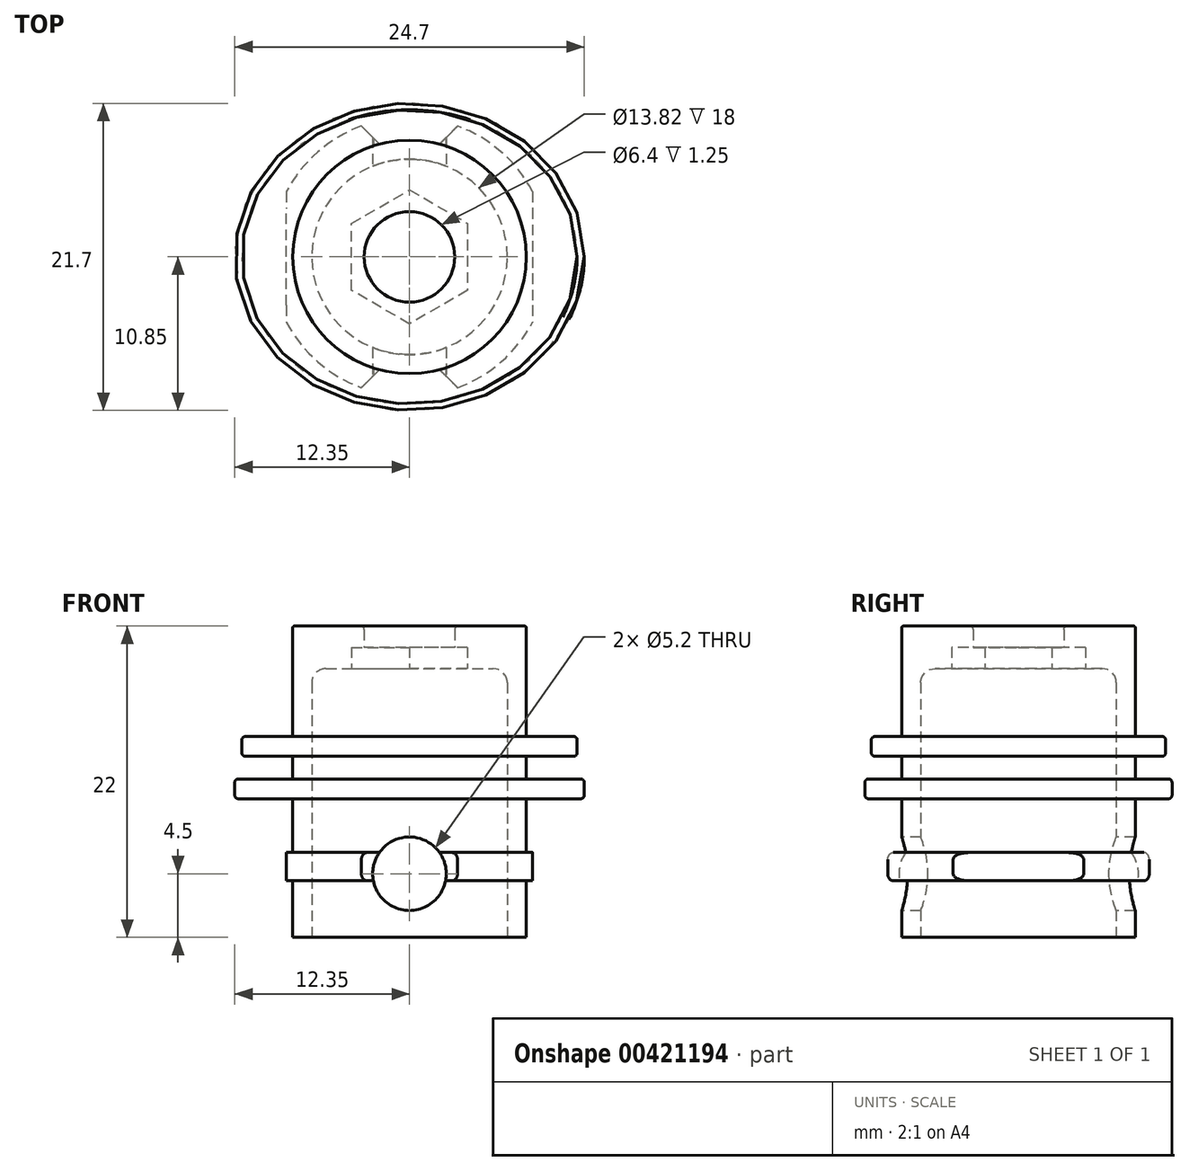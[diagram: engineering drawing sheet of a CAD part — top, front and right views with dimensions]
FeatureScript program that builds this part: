
annotation { "Feature Type Name" : "Feature", "Feature Type Description" : "" }
export const myFeature = defineFeature(function(context is Context, id is Id, definition is map)
    precondition{}
    {
        {
            var Q0;
            Q0=qCreatedBy(makeId("Front.planeOp"),FACE);
            var sketch = newSketch(context, id + "F0", { "sketchPlane" : qUnion([Q0])});
            skLineSegment(sketch, "E0", {"start": v(3.2, 19) * mm, "end": v(5.9, 19) * mm});
            skLineSegment(sketch, "E1", {"start": v(6.9, 18) * mm, "end": v(6.9, 0) * mm});
            skLineSegment(sketch, "E2", {"start": v(6.9, 0) * mm, "end": v(8.25, 0) * mm});
            skLineSegment(sketch, "E3", {"start": v(8.25, 0) * mm, "end": v(8.25, 4) * mm});
            skLineSegment(sketch, "E4", {"start": v(8.25, 4) * mm, "end": v(9.35, 4) * mm});
            skLineSegment(sketch, "E5", {"start": v(9.85, 4.5) * mm, "end": v(9.85, 5.5) * mm});
            skLineSegment(sketch, "E6", {"start": v(9.35, 6) * mm, "end": v(8.25, 6) * mm});
            skLineSegment(sketch, "E7", {"start": v(8.25, 6) * mm, "end": v(8.25, 9.8) * mm});
            skLineSegment(sketch, "E8", {"start": v(8.15, 22) * mm, "end": v(3.2, 22) * mm});
            skLineSegment(sketch, "E9", {"start": v(0, 19) * mm, "end": v(0, 22) * mm});
            skLineSegment(sketch, "E10", {"start": v(3.2, 22) * mm, "end": v(3.2, 19) * mm});
            skPoint(sketch, "E11.visualSharp", {"position": v(9.85, 6) * mm});
            skArc(sketch, "E11.filletArc", {"start": v(9.85, 5.5) * mm, "mid": v(9.7, 5.85) * mm, "end": v(9.35, 6) * mm});
            skPoint(sketch, "E12.visualSharp", {"position": v(9.85, 4) * mm});
            skArc(sketch, "E12.filletArc", {"start": v(9.35, 4) * mm, "mid": v(9.7, 4.15) * mm, "end": v(9.85, 4.5) * mm});
            skPoint(sketch, "E13.visualSharp", {"position": v(8.25, 22) * mm});
            skArc(sketch, "E13.filletArc", {"start": v(8.25, 21.9) * mm, "mid": v(8.22, 21.97) * mm, "end": v(8.15, 22) * mm});
            skPoint(sketch, "E14.visualSharp", {"position": v(6.9, 19) * mm});
            skArc(sketch, "E14.filletArc", {"start": v(6.9, 18) * mm, "mid": v(6.62, 18.7) * mm, "end": v(5.9, 19) * mm});
            skLineSegment(sketch, "E15", {"start": v(8.25, 9.8) * mm, "end": v(12.35, 9.8) * mm});
            skLineSegment(sketch, "E16", {"start": v(12.35, 9.8) * mm, "end": v(12.35, 11.2) * mm});
            skLineSegment(sketch, "E17", {"start": v(12.35, 11.2) * mm, "end": v(8.25, 11.2) * mm});
            skLineSegment(sketch, "E18.trimOffspring", {"start": v(8.25, 11.2) * mm, "end": v(8.25, 12.8) * mm});
            skLineSegment(sketch, "E19", {"start": v(8.25, 12.8) * mm, "end": v(11.85, 12.8) * mm});
            skLineSegment(sketch, "E20", {"start": v(11.85, 12.8) * mm, "end": v(11.85, 14.2) * mm});
            skLineSegment(sketch, "E21", {"start": v(11.85, 14.2) * mm, "end": v(8.25, 14.2) * mm});
            skLineSegment(sketch, "E22.trimOffspring", {"start": v(8.25, 14.2) * mm, "end": v(8.25, 21.9) * mm});
            skSolve(sketch);
        }
        {
            var Q0;
            Q0 = qSketchRegion(id + "F0", true);
            var Q1;
            Q1=sQuery(id+"F0.wireOp",EDGE,"E9");
            revolve(context, id + "F1", {"entities" : qUnion([Q0]), "axis" : qUnion([Q1]), "revolveType" : RevolveType.FULL});
        }
        {
            var Q0;
            Q0=qCreatedBy(makeId("Front.planeOp"),FACE);
            var sketch = newSketch(context, id + "F2", { "sketchPlane" : qUnion([Q0])});
            skPoint(sketch, "E23", {"position": v(0, 4.5) * mm});
            skCircle(sketch, "E24", {"center": v(0, 4.5) * mm, "radius": 2.6 * mm});
            skSolve(sketch);
        }
        {
            var Q0;
            Q0 = qSketchRegion(id + "F2", true);
            extrude(context, id + "F3", {"entities" : qUnion([Q0]), "operationType" : NewBodyOperationType.REMOVE, "oppositeDirection" : true, "depth" : 25 * mm, "hasSecondDirection" : true, "secondDirectionOppositeDirection" : false, "secondDirectionDepth" : 25 * mm});
        }
        {
            var Q0;
            Q0=qCreatedBy(makeId("Top.planeOp"),FACE);
            var sketch = newSketch(context, id + "F4", { "sketchPlane" : qUnion([Q0])});
            skLineSegment(sketch, "E25.left", {"start": v(-8.7, 12) * mm, "end": v(-8.7, -12) * mm});
            skLineSegment(sketch, "E25.right", {"start": v(8.7, 12) * mm, "end": v(8.7, -12) * mm});
            skPoint(sketch, "E25.middle", {"position": v(0, 0) * mm});
            skLineSegment(sketch, "E26", {"start": v(-8.7, 12) * mm, "end": v(-18.7, 12) * mm});
            skLineSegment(sketch, "E27", {"start": v(-18.7, -12) * mm, "end": v(-8.7, -12) * mm});
            skLineSegment(sketch, "E28", {"start": v(-18.7, 12) * mm, "end": v(-18.7, -12) * mm});
            skLineSegment(sketch, "E29", {"start": v(8.7, 12) * mm, "end": v(18.7, 12) * mm});
            skLineSegment(sketch, "E30", {"start": v(18.7, 12) * mm, "end": v(18.7, -12) * mm});
            skLineSegment(sketch, "E31", {"start": v(18.7, -12) * mm, "end": v(8.7, -12) * mm});
            skSolve(sketch);
        }
        {
            var Q0;
            Q0=makeQuery(id+"F4.imprint","IMPRINT",FACE,{"disambiguationData":[TD([[makeQuery(id+"F4.imprint","IMPRINT",EDGE,{"derivedFrom":sQuery(id+"F4.wireOp",EDGE,"E25.left")}),-1.0]])]});
            var Q1;
            Q1=makeQuery(id+"F4.imprint","IMPRINT",FACE,{"disambiguationData":[TD([[makeQuery(id+"F4.imprint","IMPRINT",EDGE,{"derivedFrom":sQuery(id+"F4.wireOp",EDGE,"E25.right")}),1.0]])]});
            extrude(context, id + "F5", {"entities" : qUnion([Q0, Q1]), "operationType" : NewBodyOperationType.REMOVE, "flatOperationType" : FlatOperationType.REMOVE, "offsetDistance" : 25 * mm, "depth" : 7 * mm, "domain" : OperationDomain.MODEL});
        }
        {
            var Q0;
            Q0=qCreatedBy(makeId("Top.planeOp"),FACE);
            var sketch = newSketch(context, id + "F6", { "sketchPlane" : qUnion([Q0])});
            skLineSegment(sketch, "E32", {"start": v(-2.12, 7.97) * mm, "end": v(-6.37, 12.21) * mm});
            skLineSegment(sketch, "E33", {"start": v(2.12, 7.97) * mm, "end": v(6.37, 12.21) * mm});
            skLineSegment(sketch, "E34", {"start": v(2.12, -7.97) * mm, "end": v(6.37, -12.21) * mm});
            skLineSegment(sketch, "E35", {"start": v(-2.12, -7.97) * mm, "end": v(-6.37, -12.21) * mm});
            skLineSegment(sketch, "E36", {"start": v(-6.37, 12.21) * mm, "end": v(6.37, 12.21) * mm});
            skLineSegment(sketch, "E37", {"start": v(-6.37, -12.21) * mm, "end": v(6.37, -12.21) * mm});
            skArc(sketch, "E38", {"start": v(2.12, 7.97) * mm, "mid": v(0, 8.25) * mm, "end": v(-2.12, 7.97) * mm});
            skArc(sketch, "E39", {"start": v(-2.12, -7.97) * mm, "mid": v(0, -8.25) * mm, "end": v(2.12, -7.97) * mm});
            skSolve(sketch);
        }
        {
            var Q0;
            Q0=makeQuery(id+"F6.imprint","IMPRINT",FACE,{"disambiguationData":[TD([[makeQuery(id+"F6.imprint","IMPRINT",EDGE,{"derivedFrom":sQuery(id+"F6.wireOp",EDGE,"E32")}),-1.0]])]});
            var Q1;
            Q1=makeQuery(id+"F6.imprint","IMPRINT",FACE,{"disambiguationData":[TD([[makeQuery(id+"F6.imprint","IMPRINT",EDGE,{"derivedFrom":sQuery(id+"F6.wireOp",EDGE,"E34")}),-1.0]])]});
            extrude(context, id + "F7", {"entities" : qUnion([Q0, Q1]), "operationType" : NewBodyOperationType.REMOVE, "depth" : 6 * mm});
        }
        {
            var Q0;
            Q0=qCreatedBy(makeId("Top.planeOp"),FACE);
            var sketch = newSketch(context, id + "F8", { "sketchPlane" : qUnion([Q0])});
            skCircle(sketch, "E40.cCircle", {"center": v(0, 0) * mm, "radius": 4.73 * mm, "construction": true});
            skLineSegment(sketch, "E40.0", {"start": v(4.1, -2.37) * mm, "end": v(0, -4.73) * mm});
            skLineSegment(sketch, "E40.1", {"start": v(0, -4.73) * mm, "end": v(-4.1, -2.37) * mm});
            skLineSegment(sketch, "E40.2", {"start": v(-4.1, -2.37) * mm, "end": v(-4.1, 2.37) * mm});
            skLineSegment(sketch, "E40.3", {"start": v(-4.1, 2.37) * mm, "end": v(0, 4.73) * mm});
            skLineSegment(sketch, "E40.4", {"start": v(0, 4.73) * mm, "end": v(4.1, 2.37) * mm});
            skLineSegment(sketch, "E40.5", {"start": v(4.1, 2.37) * mm, "end": v(4.1, -2.37) * mm});
            skSolve(sketch);
        }
        {
            var Q0;
            Q0 = qSketchRegion(id + "F8", true);
            extrude(context, id + "F9", {"entities" : qUnion([Q0]), "operationType" : NewBodyOperationType.REMOVE, "depth" : 20.5 * mm});
        }
        {
            var Q0;
            Q0=qCreatedBy(makeId("Top.planeOp"),FACE);
            var sketch = newSketch(context, id + "F10", { "sketchPlane" : qUnion([Q0])});
            skEllipse(sketch, "E41", {"center": v(0, 0) * mm, "majorRadius": 12.35 * mm, "minorRadius": 10.85 * mm, "majorAxis": v(1, 0)});
            skCircle(sketch, "E42", {"center": v(0, 0) * mm, "radius": 16.7 * mm});
            skSolve(sketch);
        }
        {
            var Q0;
            Q0=makeQuery(id+"F10.imprint","IMPRINT",FACE,{"disambiguationData":[TD([[makeQuery(id+"F10.imprint","IMPRINT",EDGE,{"derivedFrom":sQuery(id+"F10.wireOp",EDGE,"E41")}),-1.0]])]});
            extrude(context, id + "F11", {"entities" : qUnion([Q0]), "operationType" : NewBodyOperationType.REMOVE, "depth" : 12 * mm});
        }
        {
            var Q0;
            Q0=qCreatedBy(makeId("Top.planeOp"),FACE);
            var sketch = newSketch(context, id + "F12", { "sketchPlane" : qUnion([Q0])});
            skEllipse(sketch, "E43", {"center": v(0, 0) * mm, "majorRadius": 11.85 * mm, "minorRadius": 10.4 * mm, "majorAxis": v(1, 0)});
            skCircle(sketch, "E44", {"center": v(0, 0) * mm, "radius": 16.92 * mm});
            skSolve(sketch);
        }
        {
            var Q0;
            Q0=makeQuery(id+"F12.imprint","IMPRINT",FACE,{"disambiguationData":[TD([[makeQuery(id+"F12.imprint","IMPRINT",EDGE,{"derivedFrom":sQuery(id+"F12.wireOp",EDGE,"E43")}),-1.0]])]});
            extrude(context, id + "F13", {"entities" : qUnion([Q0]), "operationType" : NewBodyOperationType.REMOVE, "depth" : 25 * mm, "hasSecondDirection" : true, "secondDirectionOppositeDirection" : false, "secondDirectionDepth" : 12 * mm});
        }
        {
            var Q0;
            Q0=makeQuery(id+"F13.boolean.opBoolean","INTERSECT",EDGE,{"derivedFrom":[makeQuery(id+"F1.opRevolve","SWEPT_FACE",FACE,{"disambiguationData":[OSD([sQuery(id+"F0.wireOp",EDGE,"E21")])]}),makeQuery(id+"F13.opExtrude","SWEPT_FACE",FACE,{"disambiguationData":[OSD([sQuery(id+"F12.wireOp",EDGE,"E43")])]})]});
            var Q1;
            Q1=makeQuery(id+"F13.boolean.opBoolean","INTERSECT",EDGE,{"derivedFrom":[makeQuery(id+"F1.opRevolve","SWEPT_FACE",FACE,{"disambiguationData":[OSD([sQuery(id+"F0.wireOp",EDGE,"E19")])]}),makeQuery(id+"F13.opExtrude","SWEPT_FACE",FACE,{"disambiguationData":[OSD([sQuery(id+"F12.wireOp",EDGE,"E43")])]})]});
            var Q2;
            Q2=makeQuery(id+"F11.boolean.opBoolean","INTERSECT",EDGE,{"derivedFrom":[makeQuery(id+"F1.opRevolve","SWEPT_FACE",FACE,{"disambiguationData":[OSD([sQuery(id+"F0.wireOp",EDGE,"E17")])]}),makeQuery(id+"F11.opExtrude","SWEPT_FACE",FACE,{"disambiguationData":[OSD([sQuery(id+"F10.wireOp",EDGE,"E41")])]})]});
            var Q3;
            Q3=makeQuery(id+"F11.boolean.opBoolean","INTERSECT",EDGE,{"derivedFrom":[makeQuery(id+"F1.opRevolve","SWEPT_FACE",FACE,{"disambiguationData":[OSD([sQuery(id+"F0.wireOp",EDGE,"E15")])]}),makeQuery(id+"F11.opExtrude","SWEPT_FACE",FACE,{"disambiguationData":[OSD([sQuery(id+"F10.wireOp",EDGE,"E41")])]})]});
            fillet(context, id + "F14", {"entities" : qUnion([Q0, Q1, Q2, Q3]), "radius" : 0.25 * mm, "tangentPropagation" : true, "allowEdgeOverflow" : false});
        }
        {
            var Q0;
            Q0=makeQuery(id+"F1.opRevolve","SWEPT_EDGE",EDGE,{"disambiguationData":[OSD([sQuery(id+"F0.wireOp",EDGE,"E8"),sQuery(id+"F0.wireOp",EDGE,"E10")])]});
            fillet(context, id + "F15", {"entities" : qUnion([Q0]), "radius" : 0.25 * mm, "tangentPropagation" : true, "allowEdgeOverflow" : false});
        }
    });
